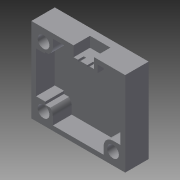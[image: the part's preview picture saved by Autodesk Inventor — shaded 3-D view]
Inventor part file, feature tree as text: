
AUTODESK INVENTOR PART (.ipt)
format: ipt  version: 2015 SP1 (Build 190203100, 203)  size: 230,912 bytes
history: native  units: mm
features: extrude x5, sketch x3, other x1, projected_geometry x1
ambient origin geometry x8: Origin, YZ Plane, XZ Plane, XY Plane, X Axis, Y Axis, Z Axis, Center Point
bodies: Body1 (feature_tree)
feature tree (10):
  other  "Твердое тело1"
  sketch  "Эскиз1"
  extrude  "Выдавливание1"  Depth=36.0mm
  extrude  "Выдавливание2"  Depth=32.0mm
  extrude  "Выдавливание3"  Depth=3.18mm
  extrude  "Выдавливание4"  Depth=3.18mm
  extrude  "Выдавливание5"  Depth=3.18mm
  sketch  "Эскиз2"
  sketch  "Эскиз4"
  projected_geometry  "Спроецированная петля1"
